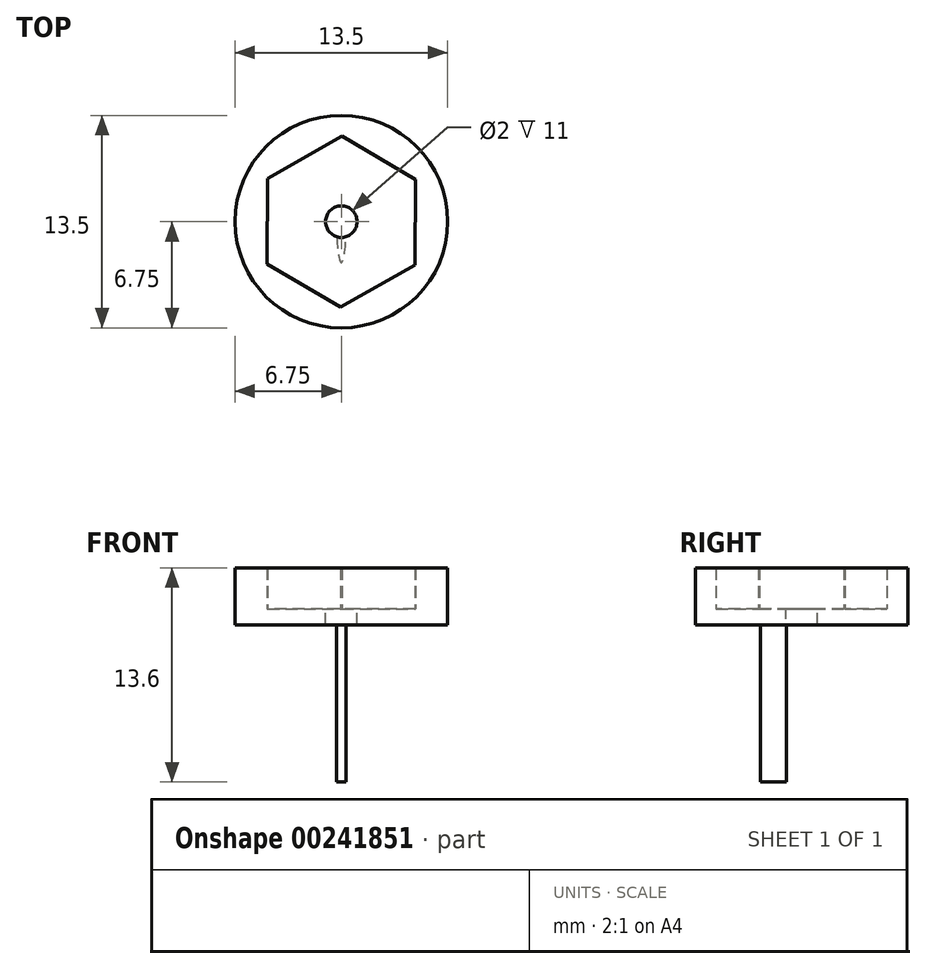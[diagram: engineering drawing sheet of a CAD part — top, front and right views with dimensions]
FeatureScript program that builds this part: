
annotation { "Feature Type Name" : "Feature", "Feature Type Description" : "" }
export const myFeature = defineFeature(function(context is Context, id is Id, definition is map)
    precondition{}
    {
        {
            var Q0;
            Q0=qCreatedBy(makeId("Top.planeOp"),FACE);
            var sketch = newSketch(context, id + "F0", { "sketchPlane" : qUnion([Q0])});
            skCircle(sketch, "E0", {"center": v(0, 0) * mm, "radius": 6.75 * mm});
            skCircle(sketch, "E1.cCircle", {"center": v(0, 0) * mm, "radius": 4.7 * mm, "construction": true});
            skLineSegment(sketch, "E1.0", {"start": v(0.04, 5.43) * mm, "end": v(4.72, 2.68) * mm});
            skLineSegment(sketch, "E1.1", {"start": v(4.72, 2.68) * mm, "end": v(4.68, -2.75) * mm});
            skLineSegment(sketch, "E1.2", {"start": v(4.68, -2.75) * mm, "end": v(-0.04, -5.43) * mm});
            skLineSegment(sketch, "E1.3", {"start": v(-0.04, -5.43) * mm, "end": v(-4.72, -2.68) * mm});
            skLineSegment(sketch, "E1.4", {"start": v(-4.72, -2.68) * mm, "end": v(-4.68, 2.75) * mm});
            skLineSegment(sketch, "E1.5", {"start": v(-4.68, 2.75) * mm, "end": v(0.04, 5.43) * mm});
            skPoint(sketch, "E1.0.midPoint", {"position": v(2.38, 4.05) * mm});
            skSolve(sketch);
        }
        {
            var Q0;
            Q0 = qSketchRegion(id + "F0", true);
            extrude(context, id + "F1", {"entities" : qUnion([Q0]), "depth" : 3.6 * mm});
        }
        {
            var Q0;
            Q0=makeQuery(id+"F0.imprint","IMPRINT",FACE,{"disambiguationData":[TD([[makeQuery(id+"F0.imprint","IMPRINT",EDGE,{"derivedFrom":sQuery(id+"F0.wireOp",EDGE,"E1.0")}),-1.0]])]});
            extrude(context, id + "F2", {"entities" : qUnion([Q0]), "operationType" : NewBodyOperationType.ADD, "depth" : 1 * mm});
        }
        {
            var Q0;
            Q0=makeQuery(id+"F2.opExtrude","CAP_FACE",FACE,{"disambiguationData":[OSD([sQuery(id+"F0.wireOp",EDGE,"E1.0"),sQuery(id+"F0.wireOp",EDGE,"E1.1"),sQuery(id+"F0.wireOp",EDGE,"E1.2"),sQuery(id+"F0.wireOp",EDGE,"E1.3"),sQuery(id+"F0.wireOp",EDGE,"E1.4"),sQuery(id+"F0.wireOp",EDGE,"E1.5")])],"isStart":false});
            var sketch = newSketch(context, id + "F3", { "sketchPlane" : qUnion([Q0])});
            skCircle(sketch, "E2", {"center": v(0, 0) * mm, "radius": 1 * mm});
            skSolve(sketch);
        }
        {
            var Q0;
            Q0 = qSketchRegion(id + "F3", true);
            extrude(context, id + "F4", {"entities" : qUnion([Q0]), "operationType" : NewBodyOperationType.REMOVE, "oppositeDirection" : true, "depth" : 25 * mm});
        }
        {
            var Q0;
            Q0=makeQuery(id+"F0.imprint","IMPRINT",FACE,{"disambiguationData":[TD([[makeQuery(id+"F0.imprint","IMPRINT",EDGE,{"derivedFrom":sQuery(id+"F0.wireOp",EDGE,"E0")}),1.0]])]});
            var sketch = newSketch(context, id + "F5", { "sketchPlane" : qUnion([Q0])});
            skCircle(sketch, "E3", {"center": v(0, 0) * mm, "radius": 3.5 * mm});
            skLineSegment(sketch, "E4", {"start": v(0, 0) * mm, "end": v(0, -2.6) * mm, "construction": true});
            skFitSpline(sketch, "E5", {"points": [v(-0.3, -0.95) * mm, v(0, -2.6) * mm, v(0.3, -0.95) * mm], "startDerivative": vector(0.26, -4.97) * mm, "endDerivative": vector(0.25, 4.96) * mm});
            skArc(sketch, "E6", {"start": v(-0.3, -0.95) * mm, "mid": v(0, -1) * mm, "end": v(0.3, -0.95) * mm});
            skSolve(sketch);
        }
        {
            var Q0;
            Q0=makeQuery(id+"F5.imprint","IMPRINT",FACE,{"disambiguationData":[TD([[makeQuery(id+"F5.imprint","IMPRINT",EDGE,{"derivedFrom":sQuery(id+"F5.wireOp",EDGE,"E5")}),1.0]])]});
            var Q1;
            Q1=sQuery(id+"F5.wireOp",EDGE,"E5");
            var Q2;
            Q2=sQuery(id+"F5.wireOp",EDGE,"E6");
            extrude(context, id + "F6", {"entities" : qUnion([Q0]), "operationType" : NewBodyOperationType.ADD, "surfaceEntities" : qUnion([Q1, Q2]), "oppositeDirection" : true, "depth" : 10 * mm});
        }
        {
            var Q0;
            Q0=qCreatedBy(makeId("Right.planeOp"),FACE);
            var sketch = newSketch(context, id + "F7", { "sketchPlane" : qUnion([Q0])});
            skLineSegment(sketch, "E7", {"start": v(0, 0) * mm, "end": v(0, 2.06) * mm, "construction": true});
            skSolve(sketch);
        }
    });
